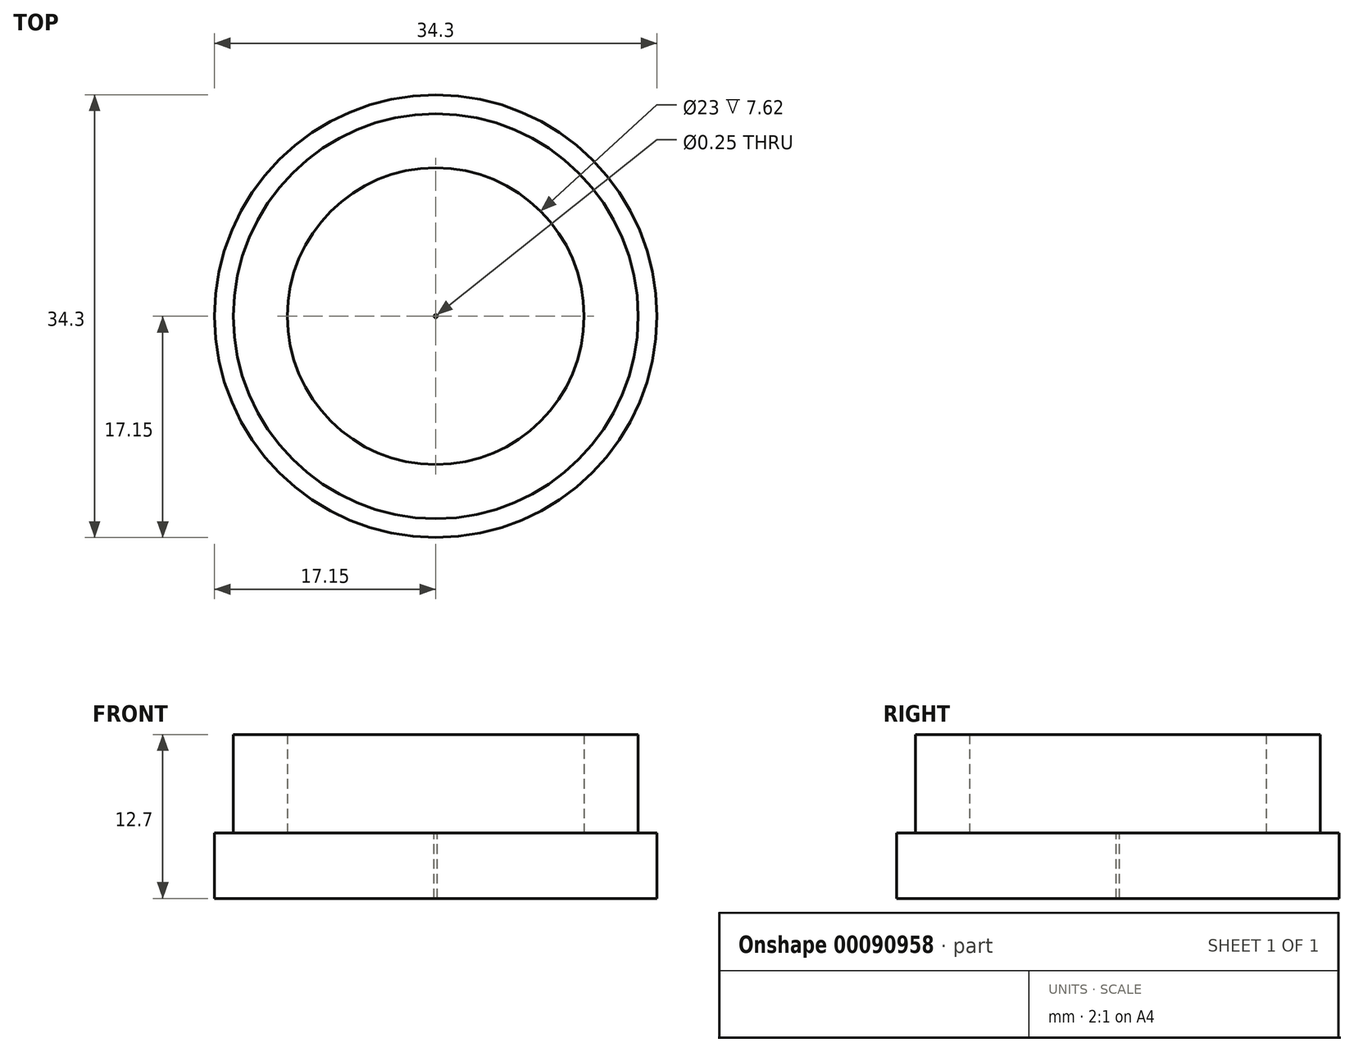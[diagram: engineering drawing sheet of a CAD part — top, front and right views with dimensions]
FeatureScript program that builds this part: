
annotation { "Feature Type Name" : "Feature", "Feature Type Description" : "" }
export const myFeature = defineFeature(function(context is Context, id is Id, definition is map)
    precondition{}
    {
        {
            var Q0;
            Q0=qCreatedBy(makeId("Top.planeOp"),FACE);
            var sketch = newSketch(context, id + "F0", { "sketchPlane" : qUnion([Q0])});
            skCircle(sketch, "E0", {"center": v(0, 0) * mm, "radius": 15.68 * mm});
            skCircle(sketch, "E1", {"center": v(0, 0) * mm, "radius": 11.5 * mm});
            skSolve(sketch);
        }
        {
            var Q0;
            Q0 = qSketchRegion(id + "F0", true);
            extrude(context, id + "F1", {"entities" : qUnion([Q0]), "depth" : 12.7 * mm});
        }
        {
            var Q0;
            Q0=qCreatedBy(makeId("Top.planeOp"),FACE);
            var sketch = newSketch(context, id + "F2", { "sketchPlane" : qUnion([Q0])});
            skCircle(sketch, "E2", {"center": v(0, 0) * mm, "radius": 17.14 * mm});
            skSolve(sketch);
        }
        {
            var Q0;
            Q0 = qSketchRegion(id + "F2", true);
            extrude(context, id + "F3", {"entities" : qUnion([Q0]), "operationType" : NewBodyOperationType.ADD, "depth" : 5.08 * mm});
        }
        {
            var Q0;
            Q0=makeQuery(id+"F3.boolean.opBoolean","SPLIT",FACE,{"disambiguationData":[TD([makeQuery(id+"F1.opExtrude","SWEPT_FACE",FACE,{"disambiguationData":[OSD([sQuery(id+"F0.wireOp",EDGE,"E1")])]})])],"derivedFrom":makeQuery(id+"F3.opExtrude","CAP_FACE",FACE,{"disambiguationData":[OSD([sQuery(id+"F2.wireOp",EDGE,"E2")])],"isStart":false})});
            var sketch = newSketch(context, id + "F4", { "sketchPlane" : qUnion([Q0])});
            skPoint(sketch, "E3", {"position": v(0, 0) * mm});
            skSolve(sketch);
        }
        {
            var Q0;
            Q0=sQuery(id+"F4.wireOp",VERTEX,"E3");
            var Q1;
            Q1=makeQuery(id+"F1.opExtrude","SWEPT_BODY",BODY,{"disambiguationData":[OSD([sQuery(id+"F0.wireOp",EDGE,"E0"),sQuery(id+"F0.wireOp",EDGE,"E1")])]});
            hole(context, id + "F5", {"style" : HoleStyle.SIMPLE, "endStyle" : HoleEndStyle.THROUGH, "holeDiameter" : 0.25 * mm, "locations" : qUnion([Q0]), "scope" : qUnion([Q1]), "isTappedThrough" : true});
        }
    });
